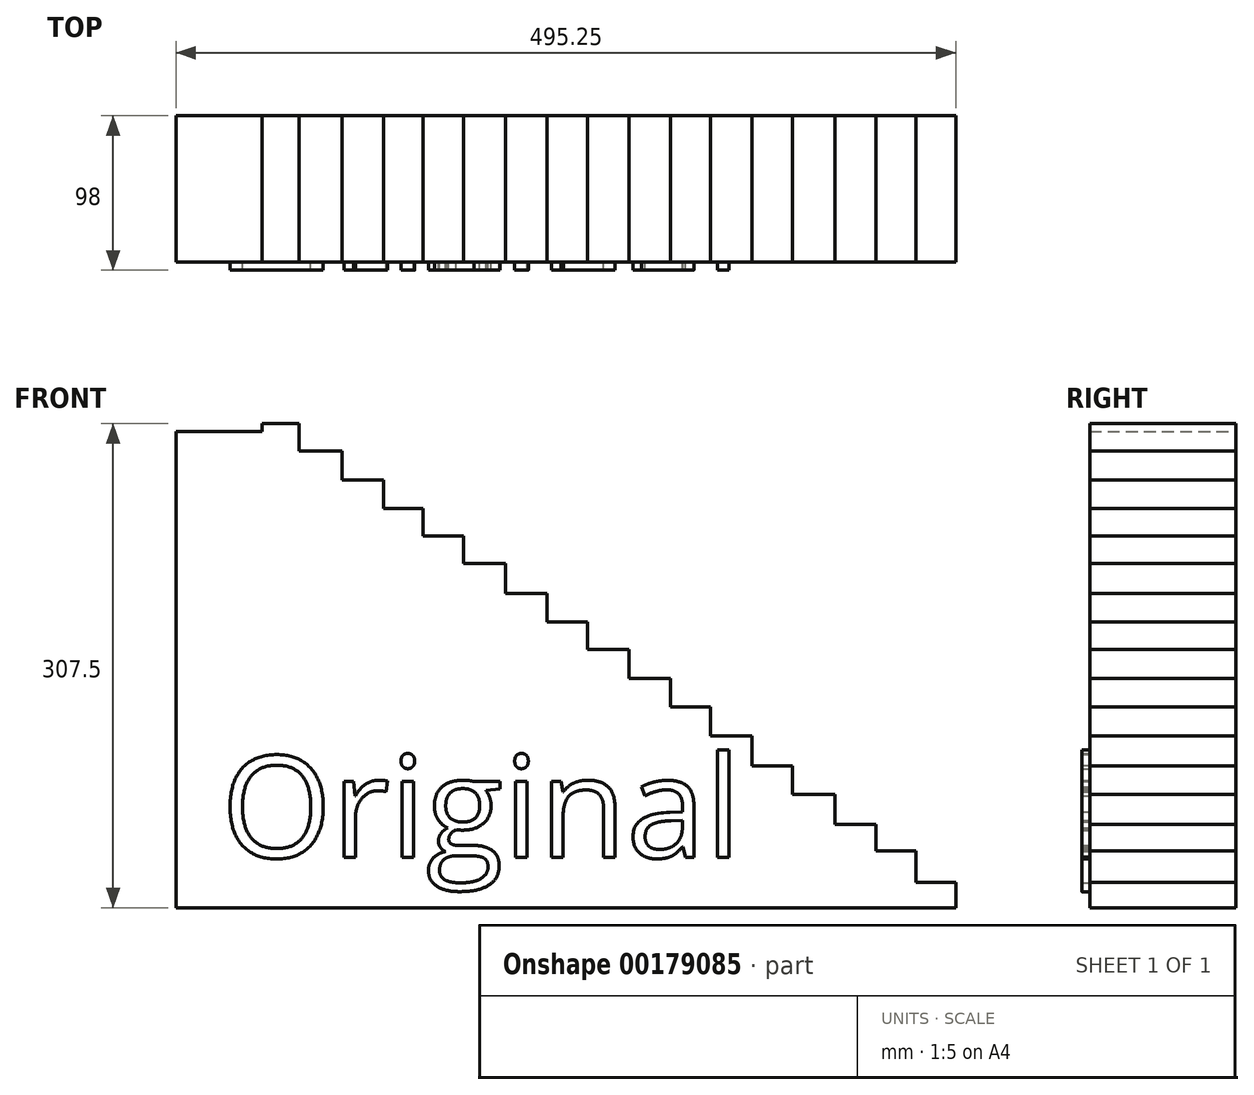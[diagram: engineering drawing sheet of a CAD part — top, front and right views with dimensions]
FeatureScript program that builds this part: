
annotation { "Feature Type Name" : "Feature", "Feature Type Description" : "" }
export const myFeature = defineFeature(function(context is Context, id is Id, definition is map)
    precondition{}
    {
        {
            var Q0;
            Q0=qCreatedBy(makeId("Front.planeOp"),FACE);
            var sketch = newSketch(context, id + "F0", { "sketchPlane" : qUnion([Q0])});
            skLineSegment(sketch, "E0", {"start": v(0, 0) * mm, "end": v(0, 0) * mm});
            skLineSegment(sketch, "E1", {"start": v(0, 0) * mm, "end": v(0, 16) * mm});
            skLineSegment(sketch, "E2", {"start": v(0, 16) * mm, "end": v(-25.4, 16) * mm});
            skLineSegment(sketch, "E3", {"start": v(-25.4, 16) * mm, "end": v(-25.4, 36) * mm});
            skLineSegment(sketch, "E4", {"start": v(-25.4, 36) * mm, "end": v(-50.9, 36) * mm});
            skLineSegment(sketch, "E5", {"start": v(-50.9, 36) * mm, "end": v(-50.9, 53) * mm});
            skLineSegment(sketch, "E6", {"start": v(-50.9, 53) * mm, "end": v(-76.7, 53) * mm});
            skLineSegment(sketch, "E7", {"start": v(-76.7, 53) * mm, "end": v(-76.7, 72) * mm});
            skLineSegment(sketch, "E8", {"start": v(-76.7, 72) * mm, "end": v(-103.8, 72) * mm});
            skLineSegment(sketch, "E9", {"start": v(-103.8, 72) * mm, "end": v(-103.8, 90) * mm});
            skLineSegment(sketch, "E10", {"start": v(-103.8, 90) * mm, "end": v(-129.5, 90) * mm});
            skLineSegment(sketch, "E11", {"start": v(-129.5, 90) * mm, "end": v(-129.5, 109) * mm});
            skLineSegment(sketch, "E12", {"start": v(-129.5, 109) * mm, "end": v(-155.7, 109) * mm});
            skLineSegment(sketch, "E13", {"start": v(-155.7, 109) * mm, "end": v(-155.7, 127.5) * mm});
            skLineSegment(sketch, "E14", {"start": v(-155.7, 127.5) * mm, "end": v(-181.4, 127.5) * mm});
            skLineSegment(sketch, "E15", {"start": v(-181.4, 127.5) * mm, "end": v(-181.4, 145.5) * mm});
            skLineSegment(sketch, "E16", {"start": v(-181.4, 145.5) * mm, "end": v(-207.7, 145.5) * mm});
            skLineSegment(sketch, "E17", {"start": v(-207.7, 145.5) * mm, "end": v(-207.7, 164) * mm});
            skLineSegment(sketch, "E18", {"start": v(-207.7, 164) * mm, "end": v(-233.8, 164) * mm});
            skLineSegment(sketch, "E19", {"start": v(-233.8, 164) * mm, "end": v(-233.8, 181.5) * mm});
            skLineSegment(sketch, "E20", {"start": v(-233.8, 181.5) * mm, "end": v(-259.8, 181.5) * mm});
            skLineSegment(sketch, "E21", {"start": v(-259.8, 181.5) * mm, "end": v(-259.8, 199.5) * mm});
            skLineSegment(sketch, "E22", {"start": v(-259.8, 199.5) * mm, "end": v(-286, 199.5) * mm});
            skLineSegment(sketch, "E23", {"start": v(-286, 199.5) * mm, "end": v(-286, 218.5) * mm});
            skLineSegment(sketch, "E24", {"start": v(-286, 218.5) * mm, "end": v(-312.7, 218.5) * mm});
            skLineSegment(sketch, "E25", {"start": v(-312.7, 218.5) * mm, "end": v(-312.7, 236) * mm});
            skLineSegment(sketch, "E26", {"start": v(-312.7, 236) * mm, "end": v(-338.4, 236) * mm});
            skLineSegment(sketch, "E27", {"start": v(-338.4, 236) * mm, "end": v(-338.4, 253.6) * mm});
            skLineSegment(sketch, "E28", {"start": v(-338.4, 253.6) * mm, "end": v(-363.4, 253.6) * mm});
            skLineSegment(sketch, "E29", {"start": v(-363.4, 253.6) * mm, "end": v(-363.4, 271.7) * mm});
            skLineSegment(sketch, "E30", {"start": v(-363.4, 271.7) * mm, "end": v(-389.7, 271.7) * mm});
            skLineSegment(sketch, "E31", {"start": v(-389.7, 271.7) * mm, "end": v(-389.7, 290.1) * mm});
            skLineSegment(sketch, "E32", {"start": v(-389.7, 290.1) * mm, "end": v(-417, 290.1) * mm});
            skLineSegment(sketch, "E33", {"start": v(0, 0) * mm, "end": v(-495.25, 0) * mm});
            skLineSegment(sketch, "E34", {"start": v(-495.25, 0) * mm, "end": v(-495.25, 302.5) * mm});
            skLineSegment(sketch, "E35", {"start": v(-417, 307.5) * mm, "end": v(113.16, 307.5) * mm});
            skLineSegment(sketch, "E36", {"start": v(-417, 290.1) * mm, "end": v(-417, 307.5) * mm});
            skLineSegment(sketch, "E37", {"start": v(-417, 307.5) * mm, "end": v(-440.65, 307.5) * mm});
            skLineSegment(sketch, "E38", {"start": v(-440.65, 307.5) * mm, "end": v(-440.65, 302.5) * mm});
            skLineSegment(sketch, "E39", {"start": v(-440.65, 302.5) * mm, "end": v(-495.25, 302.5) * mm});
            skSolve(sketch);
        }
        {
            var Q0;
            Q0=makeQuery(id+"F0.imprint","IMPRINT",FACE,{"disambiguationData":[TD([[makeQuery(id+"F0.imprint","IMPRINT",EDGE,{"derivedFrom":sQuery(id+"F0.wireOp",EDGE,"E1")}),1.0]])]});
            extrude(context, id + "F1", {"entities" : qUnion([Q0]), "depth" : 93 * mm});
        }
        {
            var Q0;
            Q0=makeQuery(id+"F1.opExtrude","CAP_FACE",FACE,{"disambiguationData":[OSD([sQuery(id+"F0.wireOp",EDGE,"E1"),sQuery(id+"F0.wireOp",EDGE,"E2"),sQuery(id+"F0.wireOp",EDGE,"E3"),sQuery(id+"F0.wireOp",EDGE,"E4"),sQuery(id+"F0.wireOp",EDGE,"E5"),sQuery(id+"F0.wireOp",EDGE,"E6"),sQuery(id+"F0.wireOp",EDGE,"E7"),sQuery(id+"F0.wireOp",EDGE,"E8"),sQuery(id+"F0.wireOp",EDGE,"E9"),sQuery(id+"F0.wireOp",EDGE,"E10"),sQuery(id+"F0.wireOp",EDGE,"E11"),sQuery(id+"F0.wireOp",EDGE,"E12"),sQuery(id+"F0.wireOp",EDGE,"E13"),sQuery(id+"F0.wireOp",EDGE,"E14"),sQuery(id+"F0.wireOp",EDGE,"E15"),sQuery(id+"F0.wireOp",EDGE,"E16"),sQuery(id+"F0.wireOp",EDGE,"E17"),sQuery(id+"F0.wireOp",EDGE,"E18"),sQuery(id+"F0.wireOp",EDGE,"E19"),sQuery(id+"F0.wireOp",EDGE,"E20"),sQuery(id+"F0.wireOp",EDGE,"E21"),sQuery(id+"F0.wireOp",EDGE,"E22"),sQuery(id+"F0.wireOp",EDGE,"E23"),sQuery(id+"F0.wireOp",EDGE,"E24"),sQuery(id+"F0.wireOp",EDGE,"E25"),sQuery(id+"F0.wireOp",EDGE,"E26"),sQuery(id+"F0.wireOp",EDGE,"E27"),sQuery(id+"F0.wireOp",EDGE,"E28"),sQuery(id+"F0.wireOp",EDGE,"E29"),sQuery(id+"F0.wireOp",EDGE,"E30"),sQuery(id+"F0.wireOp",EDGE,"E31"),sQuery(id+"F0.wireOp",EDGE,"E32"),sQuery(id+"F0.wireOp",EDGE,"E33"),sQuery(id+"F0.wireOp",EDGE,"E34"),sQuery(id+"F0.wireOp",EDGE,"E36"),sQuery(id+"F0.wireOp",EDGE,"E37"),sQuery(id+"F0.wireOp",EDGE,"E38"),sQuery(id+"F0.wireOp",EDGE,"E39")])],"isStart":false});
            var sketch = newSketch(context, id + "F2", { "sketchPlane" : qUnion([Q0])});
            skText(sketch, "E40", { "text": "Original", "fontName": "OpenSans-Regular.ttf"});
            const initialGuessF2  = {"E40": [-0.4665, 0.03186, 1, 0, 0.0649]};
            skSetInitialGuess(sketch, initialGuessF2);
            skSolve(sketch);
        }
        {
            var Q0;
            Q0 = qSketchRegion(id + "F2", true);
            extrude(context, id + "F3", {"entities" : qUnion([Q0]), "operationType" : NewBodyOperationType.ADD, "depth" : 5 * mm});
        }
    });
